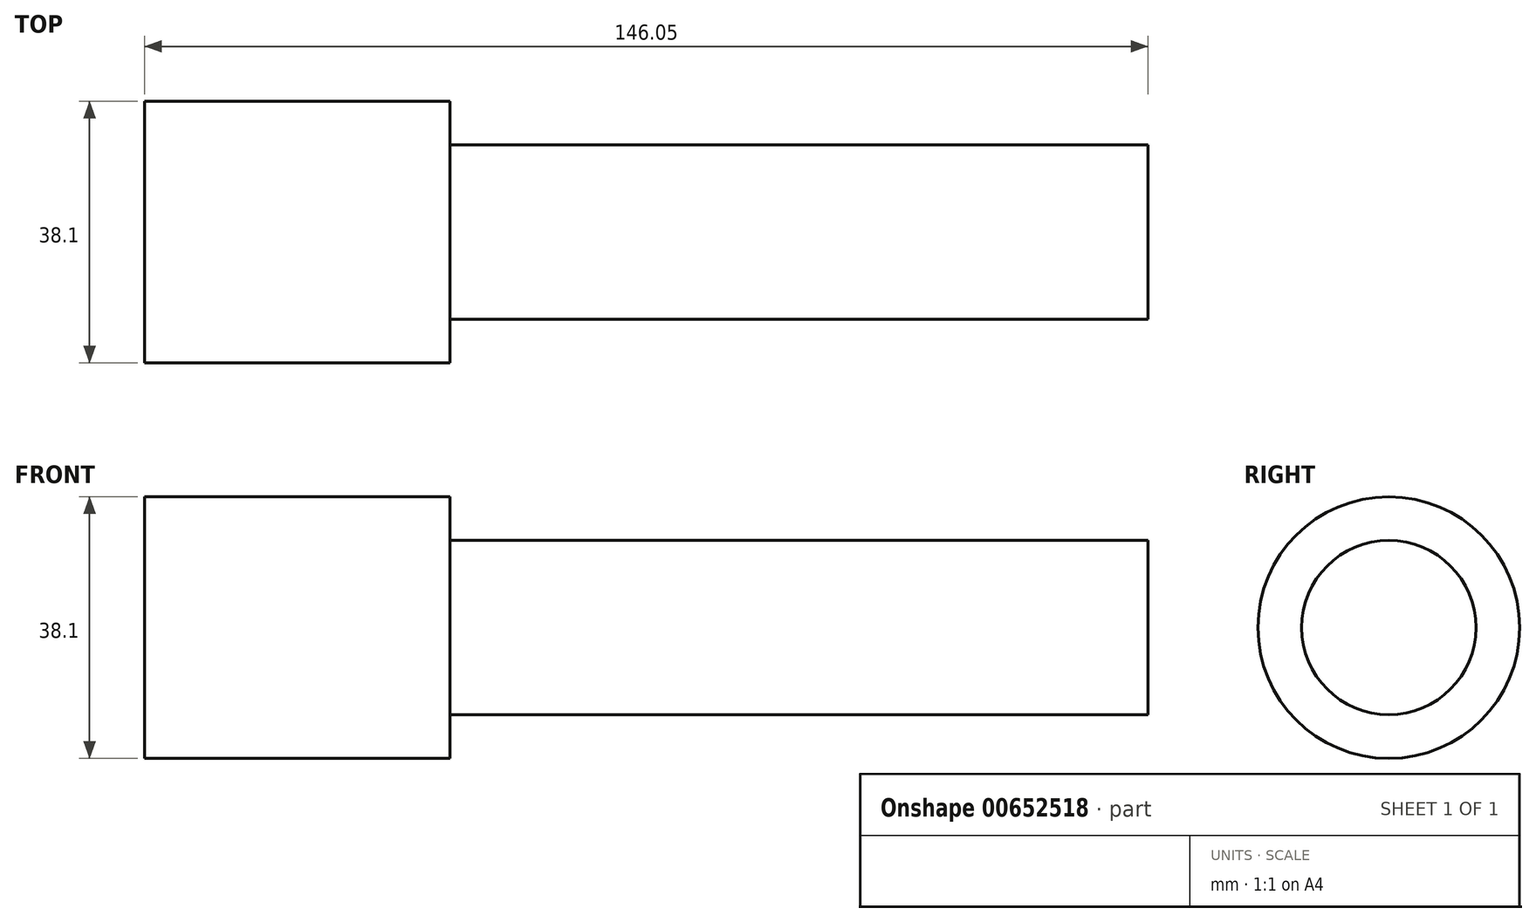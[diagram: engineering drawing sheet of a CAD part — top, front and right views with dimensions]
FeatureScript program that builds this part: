
annotation { "Feature Type Name" : "Feature", "Feature Type Description" : "" }
export const myFeature = defineFeature(function(context is Context, id is Id, definition is map)
    precondition{}
    {
        {
            var Q0;
            Q0=qCreatedBy(makeId("Right.planeOp"),FACE);
            var sketch = newSketch(context, id + "F0", { "sketchPlane" : qUnion([Q0])});
            skCircle(sketch, "E0", {"center": v(0, 0) * mm, "radius": 12.7 * mm});
            skSolve(sketch);
        }
        {
            var Q0;
            Q0=makeQuery(id+"F0.imprint","IMPRINT",FACE,{"disambiguationData":[TD([[makeQuery(id+"F0.imprint","IMPRINT",EDGE,{"derivedFrom":sQuery(id+"F0.wireOp",EDGE,"E0")}),1.0]])]});
            extrude(context, id + "F1", {"entities" : qUnion([Q0]), "depth" : 101.6 * mm, "offsetDistance" : 25.4 * mm});
        }
        {
            var Q0;
            Q0=qCreatedBy(makeId("Right.planeOp"),FACE);
            var sketch = newSketch(context, id + "F2", { "sketchPlane" : qUnion([Q0])});
            skCircle(sketch, "E1", {"center": v(0, 0) * mm, "radius": 19.05 * mm});
            skSolve(sketch);
        }
        {
            var Q0;
            Q0=makeQuery(id+"F2.imprint","IMPRINT",FACE,{"disambiguationData":[TD([[makeQuery(id+"F2.imprint","IMPRINT",EDGE,{"derivedFrom":sQuery(id+"F2.wireOp",EDGE,"E1")}),1.0]])]});
            extrude(context, id + "F3", {"entities" : qUnion([Q0]), "oppositeDirection" : true, "depth" : 44.45 * mm, "offsetDistance" : 25.4 * mm});
        }
    });
